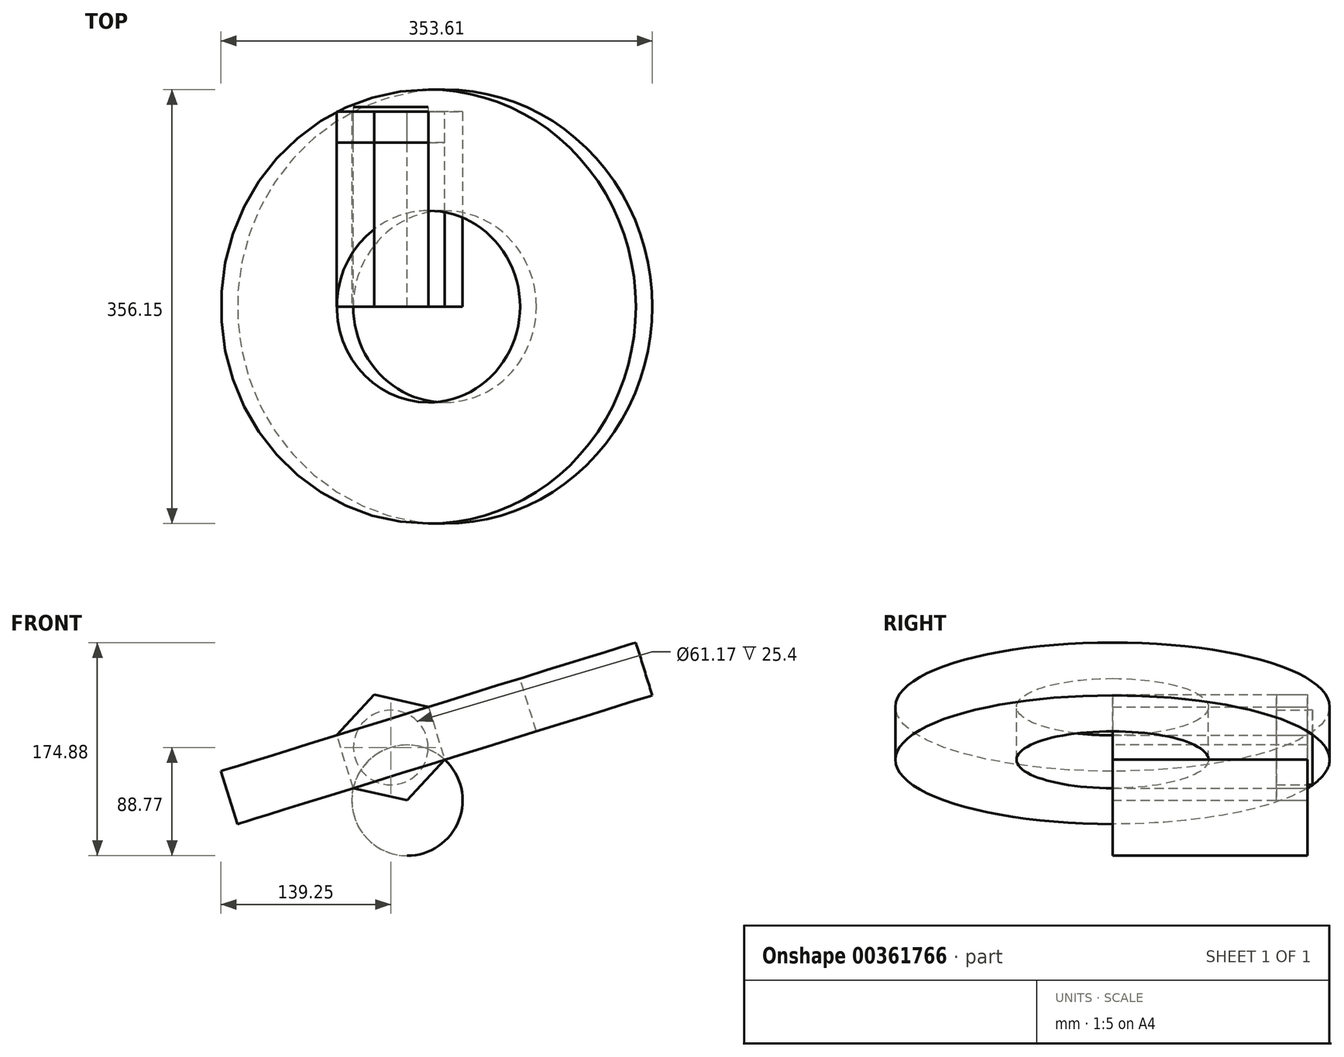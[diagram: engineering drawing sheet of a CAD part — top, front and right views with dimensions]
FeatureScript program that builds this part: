
annotation { "Feature Type Name" : "Feature", "Feature Type Description" : "" }
export const myFeature = defineFeature(function(context is Context, id is Id, definition is map)
    precondition{}
    {
        {
            var Q0;
            Q0=qCreatedBy(makeId("Front.planeOp"),FACE);
            var sketch = newSketch(context, id + "F0", { "sketchPlane" : qUnion([Q0])});
            skCircle(sketch, "E0.cCircle", {"center": v(0, 0) * mm, "radius": 39.32 * mm, "construction": true});
            skLineSegment(sketch, "E0.0", {"start": v(-30.83, -33.34) * mm, "end": v(-44.28, 10.03) * mm});
            skLineSegment(sketch, "E0.1", {"start": v(-44.28, 10.03) * mm, "end": v(-13.46, 43.36) * mm});
            skLineSegment(sketch, "E0.2", {"start": v(-13.46, 43.36) * mm, "end": v(30.83, 33.34) * mm});
            skLineSegment(sketch, "E0.3", {"start": v(30.83, 33.34) * mm, "end": v(44.28, -10.03) * mm});
            skLineSegment(sketch, "E0.4", {"start": v(44.28, -10.03) * mm, "end": v(13.46, -43.36) * mm});
            skLineSegment(sketch, "E0.5", {"start": v(13.46, -43.36) * mm, "end": v(-30.83, -33.34) * mm});
            skPoint(sketch, "E0.0.midPoint", {"position": v(-37.56, -11.65) * mm});
            skSolve(sketch);
        }
        {
            var Q0;
            Q0=makeQuery(id+"F0.imprint","IMPRINT",FACE,{"disambiguationData":[TD([[makeQuery(id+"F0.imprint","IMPRINT",EDGE,{"derivedFrom":sQuery(id+"F0.wireOp",EDGE,"E0.0")}),-1.0]])]});
            var sketch = newSketch(context, id + "F1", { "sketchPlane" : qUnion([Q0])});
            skCircle(sketch, "E1", {"center": v(0, 0) * mm, "radius": 30.59 * mm});
            skSolve(sketch);
        }
        {
            var Q0;
            Q0=makeQuery(id+"F1.imprint","IMPRINT",FACE,{"disambiguationData":[TD([[makeQuery(id+"F1.imprint","IMPRINT",EDGE,{"derivedFrom":sQuery(id+"F1.wireOp",EDGE,"E1")}),1.0]])]});
            var sketch = newSketch(context, id + "F2", { "sketchPlane" : qUnion([Q0])});
            skSolve(sketch);
        }
        {
            var Q0;
            Q0=makeQuery(id+"F1.imprint","IMPRINT",FACE,{"disambiguationData":[TD([[makeQuery(id+"F1.imprint","IMPRINT",EDGE,{"derivedFrom":sQuery(id+"F1.wireOp",EDGE,"E1")}),-1.0]])]});
            extrude(context, id + "F3", {"entities" : qUnion([Q0]), "depth" : 25.4 * mm});
        }
        {
            var Q0;
            Q0=makeQuery(id+"F2.imprint","IMPRINT",FACE,{"disambiguationData":[TD([[makeQuery(id+"F2.imprint","IMPRINT",EDGE,{"derivedFrom":makeQuery(id+"F1.imprint","IMPRINT",EDGE,{"derivedFrom":sQuery(id+"F1.wireOp",EDGE,"E1")})}),1.0]])]});
            extrude(context, id + "F4", {"entities" : qUnion([Q0]), "oppositeDirection" : true, "depth" : 4.06 * mm});
        }
        {
            var Q0;
            Q0=makeQuery(id+"F0.imprint","IMPRINT",FACE,{"disambiguationData":[TD([[makeQuery(id+"F0.imprint","IMPRINT",EDGE,{"derivedFrom":sQuery(id+"F0.wireOp",EDGE,"E0.0")}),-1.0]])]});
            extrude(context, id + "F5", {"entities" : qUnion([Q0]), "depth" : 159.77 * mm});
        }
        {
            var Q0;
            Q0=makeQuery(id+"F5.opExtrude","SWEPT_FACE",FACE,{"disambiguationData":[OSD([sQuery(id+"F0.wireOp",EDGE,"E0.5")])]});
            var Q1;
            Q1=makeQuery(id+"F5.opExtrude","SWEPT_EDGE",EDGE,{"disambiguationData":[OSD([sQuery(id+"F0.wireOp",EDGE,"E0.4"),sQuery(id+"F0.wireOp",EDGE,"E0.5")])]});
            revolve(context, id + "F6", {"entities" : qUnion([Q0]), "axis" : qUnion([Q1]), "revolveType" : RevolveType.FULL});
        }
        {
            var Q0;
            Q0=makeQuery(id+"F5.opExtrude","SWEPT_FACE",FACE,{"disambiguationData":[OSD([sQuery(id+"F0.wireOp",EDGE,"E0.0")])]});
            var Q1;
            Q1=makeQuery(id+"F5.opExtrude","CAP_EDGE",EDGE,{"disambiguationData":[OSD([sQuery(id+"F0.wireOp",EDGE,"E0.3")])],"isStart":false});
            revolve(context, id + "F7", {"entities" : qUnion([Q0]), "axis" : qUnion([Q1]), "revolveType" : RevolveType.FULL});
        }
    });
